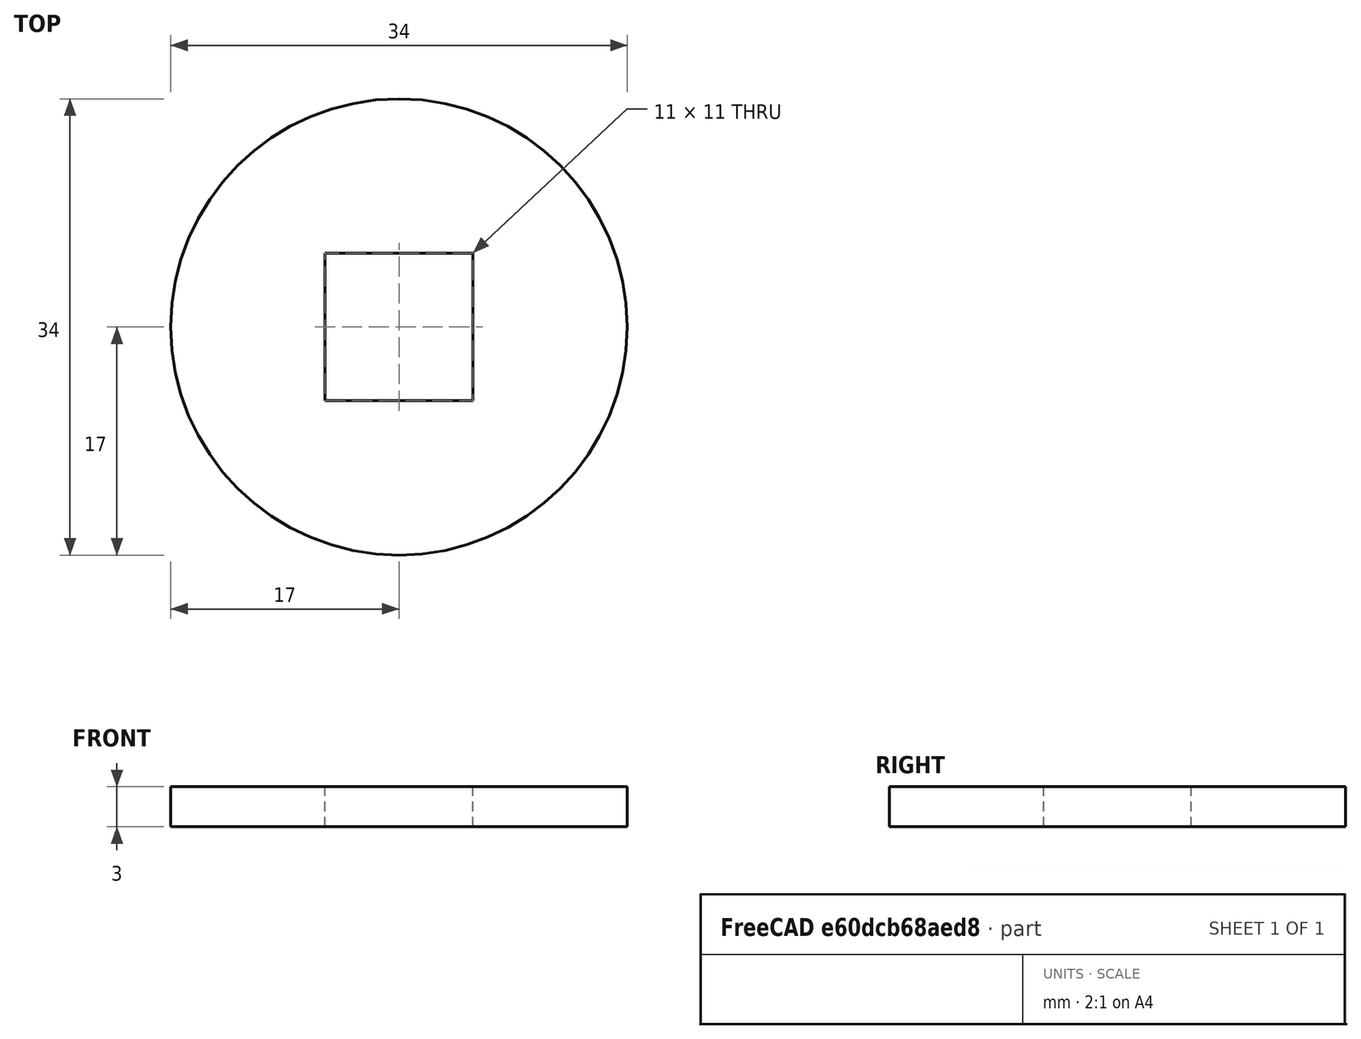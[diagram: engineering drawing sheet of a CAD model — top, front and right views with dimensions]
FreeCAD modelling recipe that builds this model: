
FCSTD DOCUMENT  (FreeCAD 0.15R4671 (Git))
Label: DIN440_CLASS_V_M10
License: CreativeCommons Attribution-ShareAlike
LicenseURL: http://creativecommons.org/licenses/by-sa/4.0/
objects: Sketcher::SketchObject×1, PartDesign::Pad×1
note: 3 computed .brp shape members not serialized (recipe doc carries the construction recipe); baked Part::Feature solids carry a one-line shape summary decoded from their .brp

FEATURE [Sketcher::SketchObject] Sketch
  sketch-geometry (5):
    g0: Circle CenterX=0 CenterY=0 CenterZ=0 NormalX=0 NormalY=0 NormalZ=1 Radius=17
    g1: LineSegment StartX=-5.5 StartY=5.5 StartZ=0 EndX=5.5 EndY=5.5 EndZ=0
    g2: LineSegment StartX=5.5 StartY=5.5 StartZ=0 EndX=5.5 EndY=-5.5 EndZ=0
    g3: LineSegment StartX=5.5 StartY=-5.5 StartZ=0 EndX=-5.5 EndY=-5.5 EndZ=0
    g4: LineSegment StartX=-5.5 StartY=-5.5 StartZ=0 EndX=-5.5 EndY=5.5 EndZ=0
  constraints (15):
    c: Coincident(g0,g-1)
    c: Radius(g0) = 17
    c: Coincident(g1,g2)
    c: Coincident(g2,g3)
    c: Coincident(g3,g4)
    c: Coincident(g4,g1)
    c: Horizontal(g1)
    c: Horizontal(g3)
    c: Vertical(g2)
    c: Vertical(g4)
    c: Equal(g1,g4)
    c: Equal(g4,g3)
    c: Equal(g3,g2)
    c: DistanceX(g1,g1) = 11
    c: Symmetric(g2,g1,g-1)
FEATURE [PartDesign::Pad] Pad
  Length = 3
  Length2 = 100
  Sketch = -> Sketch
  Type = 0
